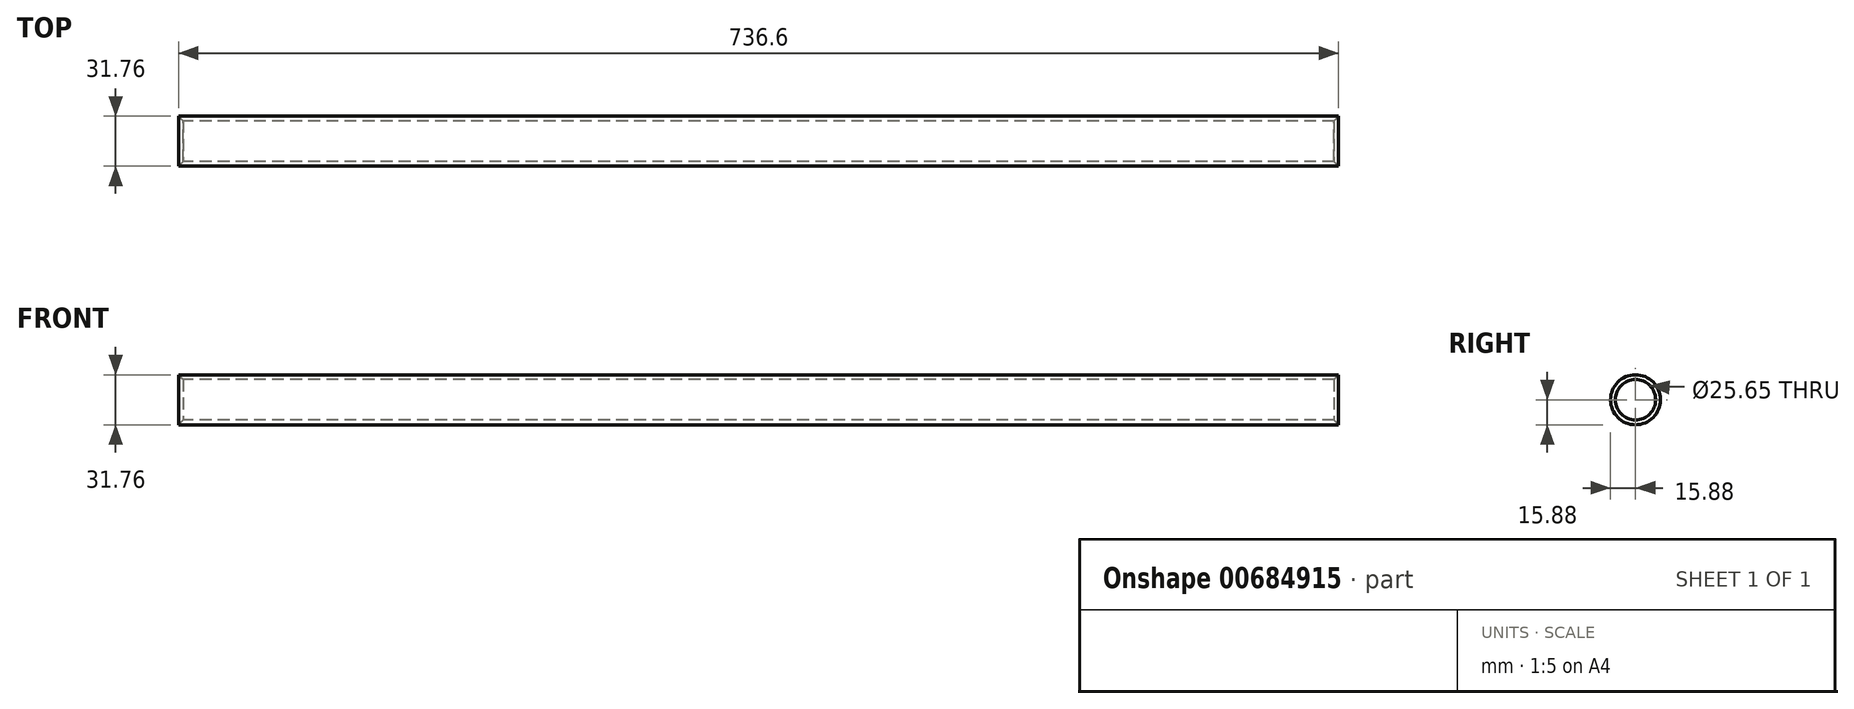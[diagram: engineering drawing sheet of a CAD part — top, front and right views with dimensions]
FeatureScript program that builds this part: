
annotation { "Feature Type Name" : "Feature", "Feature Type Description" : "" }
export const myFeature = defineFeature(function(context is Context, id is Id, definition is map)
    precondition{}
    {
        {
            var Q0;
            Q0=qCreatedBy(makeId("Front.planeOp"),FACE);
            var sketch = newSketch(context, id + "F0", { "sketchPlane" : qUnion([Q0])});
            skLineSegment(sketch, "E0", {"start": v(0, 0) * mm, "end": v(762, 0) * mm, "construction": true});
            skLineSegment(sketch, "E1", {"start": v(0, 15.88) * mm, "end": v(736.6, 15.88) * mm});
            skLineSegment(sketch, "E2", {"start": v(0, 15.88) * mm, "end": v(2.74, 12.83) * mm});
            skLineSegment(sketch, "E3", {"start": v(736.6, 15.88) * mm, "end": v(733.86, 12.83) * mm});
            skLineSegment(sketch, "E4", {"start": v(733.86, 12.83) * mm, "end": v(2.74, 12.83) * mm});
            skSolve(sketch);
        }
        {
            var Q0;
            Q0 = qSketchRegion(id + "F0", true);
            var Q1;
            Q1=sQuery(id+"F0.wireOp",EDGE,"E0");
            revolve(context, id + "F1", {"surfaceOperationType" : NewSurfaceOperationType.NEW, "entities" : qUnion([Q0]), "axis" : qUnion([Q1]), "revolveType" : RevolveType.FULL});
        }
    });
